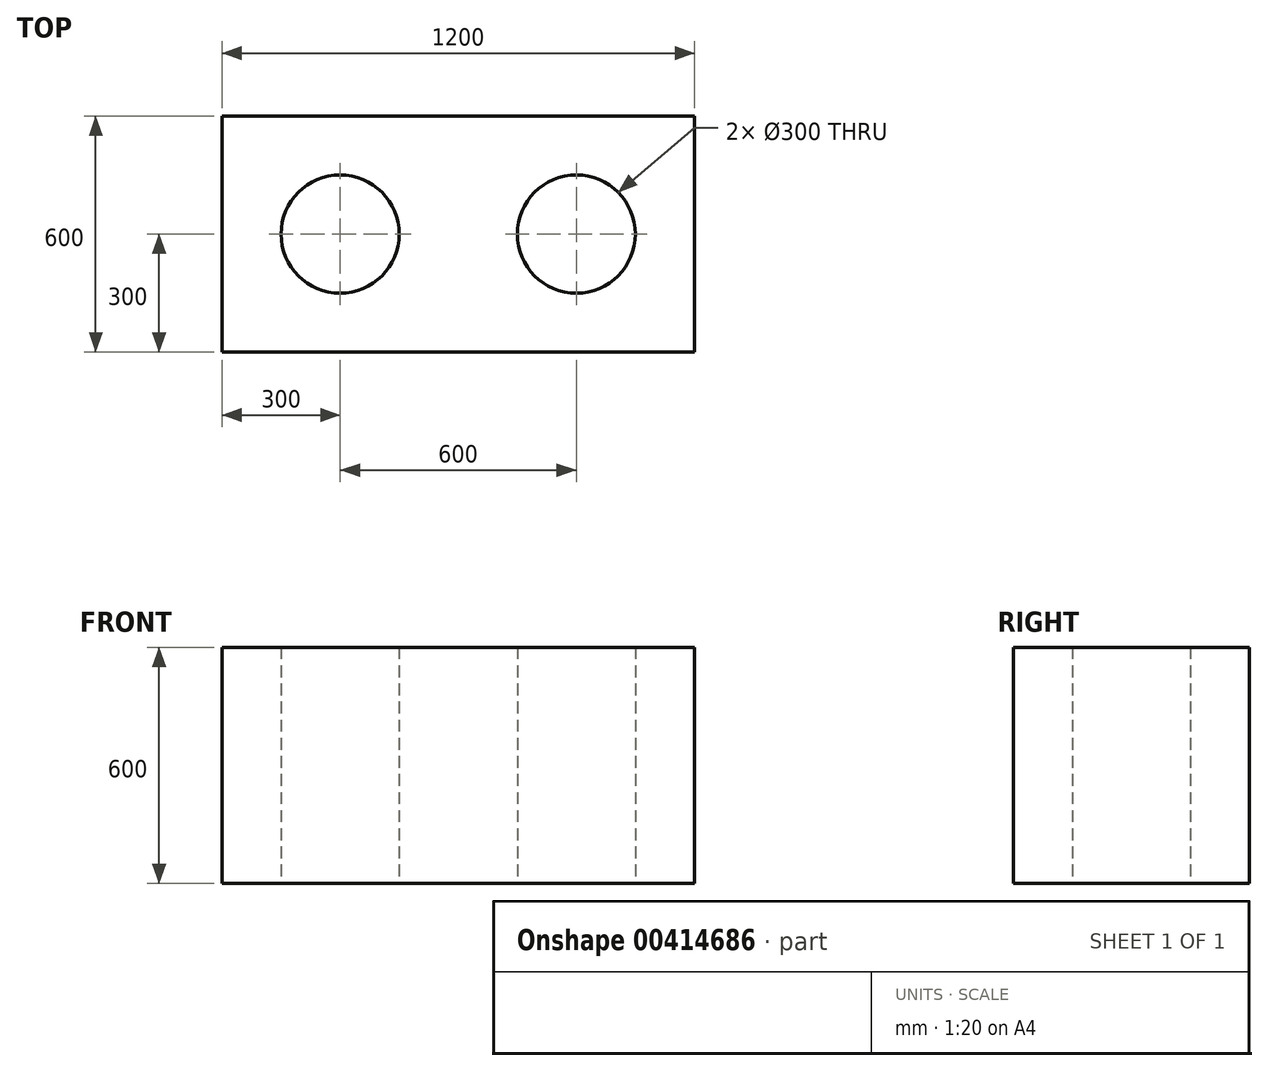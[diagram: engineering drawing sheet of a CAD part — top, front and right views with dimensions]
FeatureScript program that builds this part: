
annotation { "Feature Type Name" : "Feature", "Feature Type Description" : "" }
export const myFeature = defineFeature(function(context is Context, id is Id, definition is map)
    precondition{}
    {
        {
            var Q0;
            Q0=qCreatedBy(makeId("Top.planeOp"),FACE);
            var sketch = newSketch(context, id + "F0", { "sketchPlane" : qUnion([Q0])});
            skLineSegment(sketch, "E0", {"start": v(0, 0) * mm, "end": v(600, 0) * mm});
            skLineSegment(sketch, "E1", {"start": v(0, 0) * mm, "end": v(-600, 0) * mm});
            skLineSegment(sketch, "E2", {"start": v(-600, 0) * mm, "end": v(-600, 300) * mm});
            skLineSegment(sketch, "E3", {"start": v(-600, 0) * mm, "end": v(-600, -300) * mm});
            skLineSegment(sketch, "E4", {"start": v(-600, -300) * mm, "end": v(600, -300) * mm});
            skLineSegment(sketch, "E5", {"start": v(-600, 300) * mm, "end": v(600, 300) * mm});
            skLineSegment(sketch, "E6", {"start": v(600, 300) * mm, "end": v(600, -300) * mm});
            skLineSegment(sketch, "E7", {"start": v(-600, 0) * mm, "end": v(-300, 0) * mm});
            skLineSegment(sketch, "E8", {"start": v(600, 0) * mm, "end": v(300, 0) * mm});
            skCircle(sketch, "E9", {"center": v(-300, 0) * mm, "radius": 150 * mm});
            skCircle(sketch, "E10", {"center": v(300, 0) * mm, "radius": 150 * mm});
            skSolve(sketch);
        }
        {
            var Q0;
            {var subQ0=sQuery(id+"F0.wireOp",EDGE,"E2");Q0=makeQuery(id+"F0.imprint","IMPRINT",FACE,{"disambiguationData":[TD([[makeQuery(id+"F0.imprint","IMPRINT",EDGE,{"derivedFrom":subQ0}),-1.0]])]});}
            var Q1;
            {var subQ10=sQuery(id+"F0.wireOp",EDGE,"E3");Q1=makeQuery(id+"F0.imprint","IMPRINT",FACE,{"disambiguationData":[TD([[makeQuery(id+"F0.imprint","IMPRINT",EDGE,{"derivedFrom":subQ10}),1.0]])]});}
            extrude(context, id + "F1", {"entities" : qUnion([Q0, Q1]), "depth" : 600 * mm});
        }
    });
